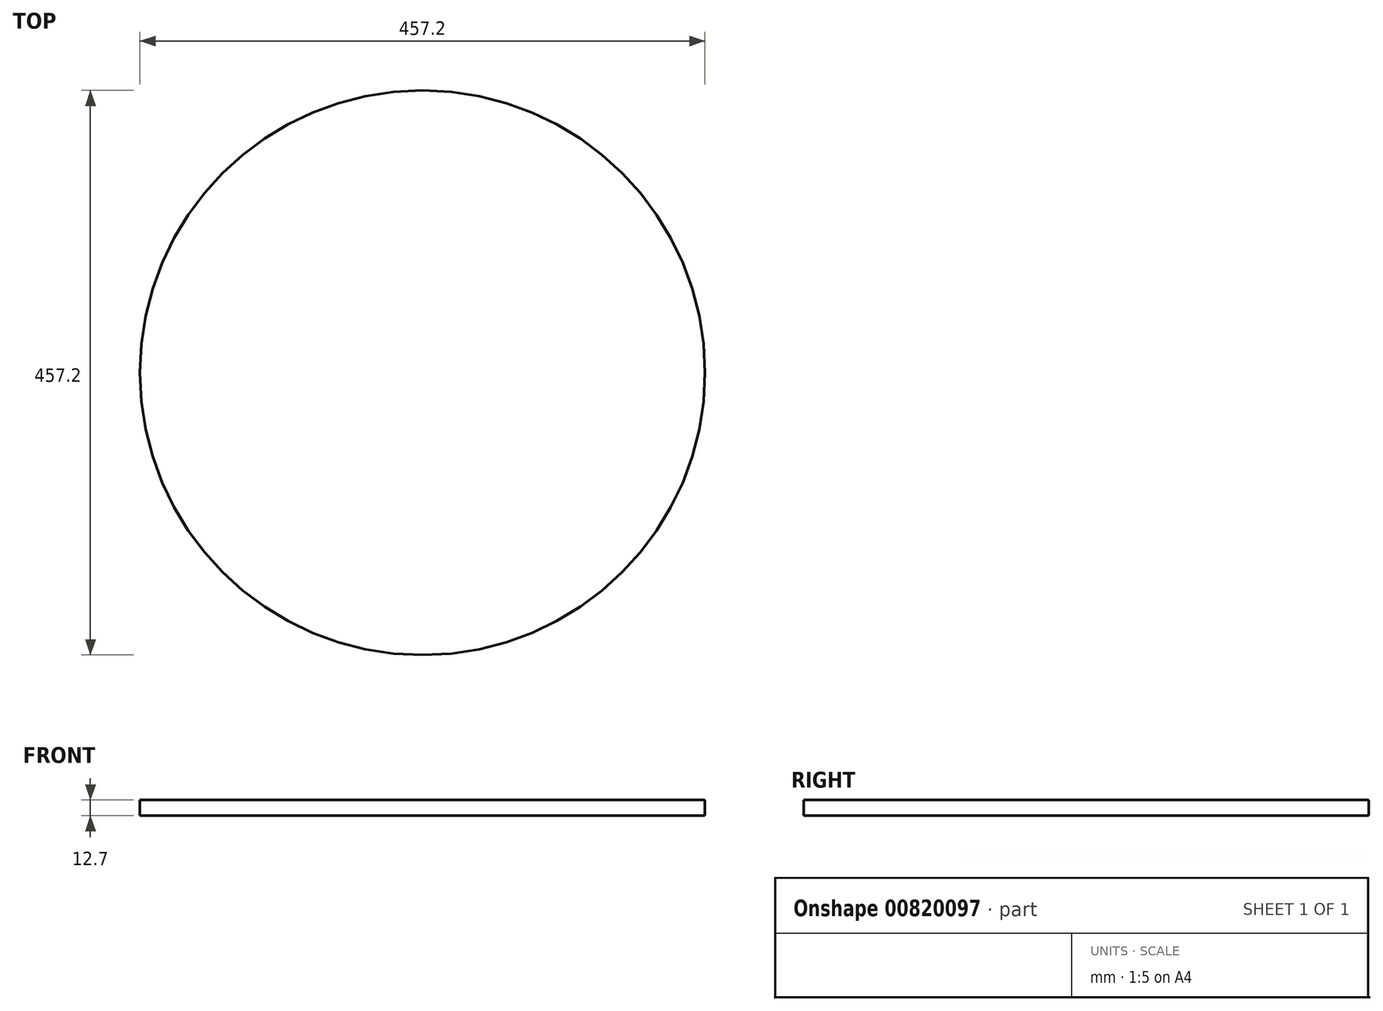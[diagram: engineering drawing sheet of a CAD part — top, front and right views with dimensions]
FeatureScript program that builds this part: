
annotation { "Feature Type Name" : "Feature", "Feature Type Description" : "" }
export const myFeature = defineFeature(function(context is Context, id is Id, definition is map)
    precondition{}
    {
        {
            var Q0;
            Q0=qCreatedBy(makeId("Top.planeOp"),FACE);
            var sketch = newSketch(context, id + "F0", { "sketchPlane" : qUnion([Q0])});
            skCircle(sketch, "E0", {"center": v(0, 0) * mm, "radius": 228.6 * mm});
            skSolve(sketch);
        }
        {
            var Q0;
            Q0 = qSketchRegion(id + "F0", true);
            extrude(context, id + "F1", {"entities" : qUnion([Q0]), "depth" : 12.7 * mm, "offsetDistance" : 25.4 * mm});
        }
    });
